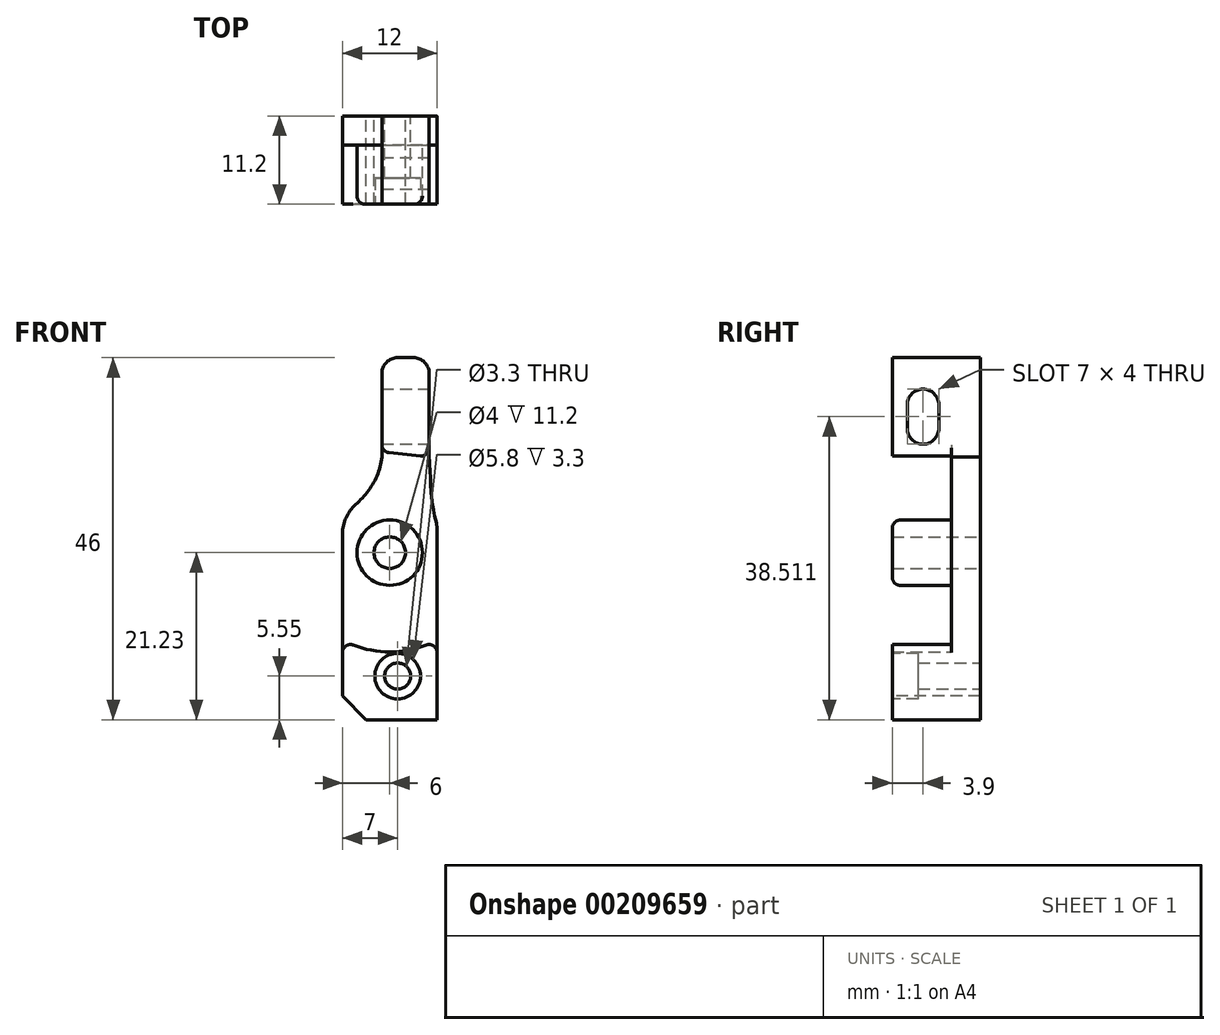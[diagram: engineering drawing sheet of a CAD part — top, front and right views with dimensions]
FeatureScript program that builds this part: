
annotation { "Feature Type Name" : "Feature", "Feature Type Description" : "" }
export const myFeature = defineFeature(function(context is Context, id is Id, definition is map)
    precondition{}
    {
        {
            var Q0;
            Q0=qCreatedBy(makeId("Front.planeOp"),FACE);
            var sketch = newSketch(context, id + "F0", { "sketchPlane" : qUnion([Q0])});
            skLineSegment(sketch, "E0.bottom", {"start": v(-1, 23) * mm, "end": v(5, 23) * mm});
            skLineSegment(sketch, "E0.top", {"start": v(-6, -23) * mm, "end": v(6, -23) * mm});
            skLineSegment(sketch, "E0.left", {"start": v(-6, 0.62) * mm, "end": v(-6, -23) * mm});
            skLineSegment(sketch, "E0.right", {"start": v(6, 1.28) * mm, "end": v(6, -23) * mm});
            skLineSegment(sketch, "E1", {"start": v(0, 12.65) * mm, "end": v(0, -11.86) * mm, "construction": true});
            skLineSegment(sketch, "E2", {"start": v(-8.9, 0) * mm, "end": v(11.6, 0) * mm, "construction": true});
            skPoint(sketch, "E2.endSnap0", {"position": v(6, 0) * mm});
            skLineSegment(sketch, "E3.left", {"start": v(-1, 23) * mm, "end": v(-1, 10.4) * mm});
            skLineSegment(sketch, "E3.right", {"start": v(5, 23) * mm, "end": v(5, 10.4) * mm});
            skCircle(sketch, "E4", {"center": v(1, -17.45) * mm, "radius": 1.65 * mm});
            skCircle(sketch, "E5", {"center": v(0, -1.77) * mm, "radius": 2 * mm});
            skFitSpline(sketch, "E6", {"points": [v(-1, 10.4) * mm, v(-6, 3.09) * mm], "startDerivative": vector(-0.84, -9.8) * mm, "endDerivative": vector(-6.83, -4.33) * mm});
            skFitSpline(sketch, "E7", {"points": [v(5, 10.4) * mm, v(6, 1.64) * mm], "startDerivative": vector(1.09, -14.14) * mm, "endDerivative": vector(3.01, -12.24) * mm});
            skPoint(sketch, "E8.orphan", {"position": v(6, 23) * mm});
            skArc(sketch, "E9.filletArc", {"start": v(-4.33, 4.35) * mm, "mid": v(-5.56, 2.67) * mm, "end": v(-6, 0.62) * mm});
            skArc(sketch, "E10.filletArc", {"start": v(6, 1.28) * mm, "mid": v(5.98, 1.64) * mm, "end": v(5.92, 1.99) * mm});
            skSolve(sketch);
        }
        {
            var Q0;
            Q0 = qSketchRegion(id + "F0", true);
            extrude(context, id + "F1", {"entities" : qUnion([Q0]), "depth" : 3.7 * mm});
        }
        {
            var Q0;
            Q0=makeQuery(id+"F1.opExtrude","CAP_FACE",FACE,{"disambiguationData":[OSD([sQuery(id+"F0.wireOp",EDGE,"E0.top"),sQuery(id+"F0.wireOp",EDGE,"E0.left"),sQuery(id+"F0.wireOp",EDGE,"E0.right"),sQuery(id+"F0.wireOp",EDGE,"E0.bottom"),sQuery(id+"F0.wireOp",EDGE,"E3.left"),sQuery(id+"F0.wireOp",EDGE,"E3.right"),sQuery(id+"F0.wireOp",EDGE,"E4"),sQuery(id+"F0.wireOp",EDGE,"E5"),sQuery(id+"F0.wireOp",EDGE,"E6"),sQuery(id+"F0.wireOp",EDGE,"E7"),sQuery(id+"F0.wireOp",EDGE,"E9.filletArc"),sQuery(id+"F0.wireOp",EDGE,"E10.filletArc")])],"isStart":false});
            var sketch = newSketch(context, id + "F2", { "sketchPlane" : qUnion([Q0])});
            skCircle(sketch, "E11", {"center": v(0, -1.77) * mm, "radius": 4.15 * mm});
            skCircle(sketch, "E12", {"center": v(0, -1.77) * mm, "radius": 2 * mm});
            skLineSegment(sketch, "E13.bottom", {"start": v(-1, 23) * mm, "end": v(5, 23) * mm});
            skLineSegment(sketch, "E13.left", {"start": v(-1, 23) * mm, "end": v(-1, 11.03) * mm});
            skLineSegment(sketch, "E13.right", {"start": v(5, 23) * mm, "end": v(5, 10.44) * mm});
            skLineSegment(sketch, "E14", {"start": v(-1, 11.03) * mm, "end": v(5, 10.4) * mm});
            skLineSegment(sketch, "E15.bottom", {"start": v(-6, -23) * mm, "end": v(6, -23) * mm});
            skLineSegment(sketch, "E15.left", {"start": v(-6, -23) * mm, "end": v(-6, -12.9) * mm});
            skLineSegment(sketch, "E15.right", {"start": v(6, -23) * mm, "end": v(6, -12.9) * mm});
            skArc(sketch, "E16", {"start": v(-6, -12.9) * mm, "mid": v(0, -14.37) * mm, "end": v(6, -12.9) * mm});
            skCircle(sketch, "E17", {"center": v(1, -17.45) * mm, "radius": 1.65 * mm});
            skSolve(sketch);
        }
        {
            var Q0;
            Q0 = qSketchRegion(id + "F2", true);
            var Q1;
            Q1=makeQuery(id+"F2.imprint","IMPRINT",FACE,{"disambiguationData":[TD([[makeQuery(id+"F2.imprint","IMPRINT",EDGE,{"derivedFrom":sQuery(id+"F2.wireOp",EDGE,"E13.bottom")}),-1.0]])]});
            extrude(context, id + "F3", {"entities" : qUnion([Q0, Q1]), "operationType" : NewBodyOperationType.ADD, "depth" : 7.5 * mm});
        }
        {
            var Q0;
            Q0=makeQuery(id+"F3.boolean.opBoolean","MERGE",EDGE,{"derivedFrom":[makeQuery(id+"F1.opExtrude","SWEPT_EDGE",EDGE,{"disambiguationData":[OSD([sQuery(id+"F0.wireOp",EDGE,"E0.bottom"),sQuery(id+"F0.wireOp",EDGE,"E3.right")])]}),makeQuery(id+"F3.opExtrude","SWEPT_EDGE",EDGE,{"disambiguationData":[OSD([sQuery(id+"F2.wireOp",EDGE,"E13.bottom"),sQuery(id+"F2.wireOp",EDGE,"E13.right")])]})]});
            var Q1;
            Q1=makeQuery(id+"F3.boolean.opBoolean","MERGE",EDGE,{"derivedFrom":[makeQuery(id+"F1.opExtrude","SWEPT_EDGE",EDGE,{"disambiguationData":[OSD([sQuery(id+"F0.wireOp",EDGE,"E0.bottom"),sQuery(id+"F0.wireOp",EDGE,"E3.left")])]}),makeQuery(id+"F3.opExtrude","SWEPT_EDGE",EDGE,{"disambiguationData":[OSD([sQuery(id+"F2.wireOp",EDGE,"E13.bottom"),sQuery(id+"F2.wireOp",EDGE,"E13.left")])]})]});
            fillet(context, id + "F4", {"entities" : qUnion([Q0, Q1]), "radius" : 2 * mm, "tangentPropagation" : true, "allowEdgeOverflow" : false});
        }
        {
            var Q0;
            Q0=makeQuery(id+"F3.opExtrude","SWEPT_EDGE",EDGE,{"disambiguationData":[OSD([sQuery(id+"F0.wireOp",EDGE,"E3.left"),sQuery(id+"F2.wireOp",EDGE,"E13.left"),sQuery(id+"F2.wireOp",EDGE,"E14")])]});
            var Q1;
            Q1=makeQuery(id+"F3.opExtrude","SWEPT_EDGE",EDGE,{"disambiguationData":[OSD([sQuery(id+"F0.wireOp",EDGE,"E3.right"),sQuery(id+"F0.wireOp",EDGE,"E7"),sQuery(id+"F2.wireOp",EDGE,"E14")])]});
            var Q2;
            Q2=makeQuery(id+"F3.opExtrude","SWEPT_EDGE",EDGE,{"disambiguationData":[OSD([sQuery(id+"F0.wireOp",EDGE,"E0.right"),sQuery(id+"F2.wireOp",EDGE,"E15.right"),sQuery(id+"F2.wireOp",EDGE,"E16")])]});
            var Q3;
            Q3=makeQuery(id+"F3.opExtrude","SWEPT_EDGE",EDGE,{"disambiguationData":[OSD([sQuery(id+"F0.wireOp",EDGE,"E0.left"),sQuery(id+"F2.wireOp",EDGE,"E15.left"),sQuery(id+"F2.wireOp",EDGE,"E16")])]});
            fillet(context, id + "F5", {"entities" : qUnion([Q0, Q1, Q2, Q3]), "radius" : 1 * mm, "tangentPropagation" : true, "allowEdgeOverflow" : false});
        }
        {
            var Q0;
            Q0=makeQuery(id+"F3.opExtrude","CAP_FACE",FACE,{"disambiguationData":[OSD([sQuery(id+"F2.wireOp",EDGE,"E15.bottom"),sQuery(id+"F2.wireOp",EDGE,"E15.left"),sQuery(id+"F2.wireOp",EDGE,"E15.right"),sQuery(id+"F2.wireOp",EDGE,"E16"),sQuery(id+"F2.wireOp",EDGE,"E17")])],"isStart":false});
            var sketch = newSketch(context, id + "F6", { "sketchPlane" : qUnion([Q0])});
            skCircle(sketch, "E18", {"center": v(1, -17.45) * mm, "radius": 2.9 * mm});
            skSolve(sketch);
        }
        {
            var Q0;
            Q0 = qSketchRegion(id + "F6", true);
            extrude(context, id + "F7", {"entities" : qUnion([Q0]), "operationType" : NewBodyOperationType.REMOVE, "oppositeDirection" : true, "depth" : 3.3 * mm});
        }
        {
            var Q0;
            Q0=makeQuery(id+"F3.opExtrude","CAP_EDGE",EDGE,{"disambiguationData":[OSD([sQuery(id+"F2.wireOp",EDGE,"E11")])],"isStart":false});
            fillet(context, id + "F8", {"entities" : qUnion([Q0]), "radius" : 1 * mm, "tangentPropagation" : true, "allowEdgeOverflow" : false});
        }
        {
            var Q0;
            {var subQ0=sQuery(id+"F0.wireOp",EDGE,"E3.right");Q0=makeQuery(id+"F3.boolean.opBoolean","MERGE",FACE,{"derivedFrom":[makeQuery(id+"F1.opExtrude","SWEPT_FACE",FACE,{"disambiguationData":[OSD([subQ0])]}),makeQuery(id+"F3.opExtrude","SWEPT_FACE",FACE,{"disambiguationData":[OSD([subQ0,sQuery(id+"F2.wireOp",EDGE,"E13.right")])]})]});}
            var sketch = newSketch(context, id + "F9", { "sketchPlane" : qUnion([Q0])});
            skArc(sketch, "E19", {"start": v(-5.3, 17.01) * mm, "mid": v(-7.3, 19.01) * mm, "end": v(-9.3, 17.01) * mm});
            skLineSegment(sketch, "E20", {"start": v(-9.3, 17.01) * mm, "end": v(-9.3, 14.01) * mm});
            skLineSegment(sketch, "E21", {"start": v(-5.3, 17.01) * mm, "end": v(-5.3, 14.01) * mm});
            skArc(sketch, "E22", {"start": v(-9.3, 14.01) * mm, "mid": v(-7.3, 12.01) * mm, "end": v(-5.3, 14.01) * mm});
            skSolve(sketch);
        }
        {
            var Q0;
            Q0 = qSketchRegion(id + "F9", true);
            extrude(context, id + "F10", {"entities" : qUnion([Q0]), "operationType" : NewBodyOperationType.REMOVE, "endBound" : BoundingType.THROUGH_ALL, "oppositeDirection" : true, "depth" : 25 * mm});
        }
        {
            var Q0;
            Q0=makeQuery(id+"F3.boolean.opBoolean","MERGE",EDGE,{"derivedFrom":[makeQuery(id+"F1.opExtrude","SWEPT_EDGE",EDGE,{"disambiguationData":[OSD([sQuery(id+"F0.wireOp",EDGE,"E0.top"),sQuery(id+"F0.wireOp",EDGE,"E0.left")])]}),makeQuery(id+"F3.opExtrude","SWEPT_EDGE",EDGE,{"disambiguationData":[OSD([sQuery(id+"F2.wireOp",EDGE,"E15.bottom"),sQuery(id+"F2.wireOp",EDGE,"E15.left")])]})]});
            chamfer(context, id + "F11", {"entities" : qUnion([Q0]), "width" : 3 * mm, "tangentPropagation" : true});
        }
    });
